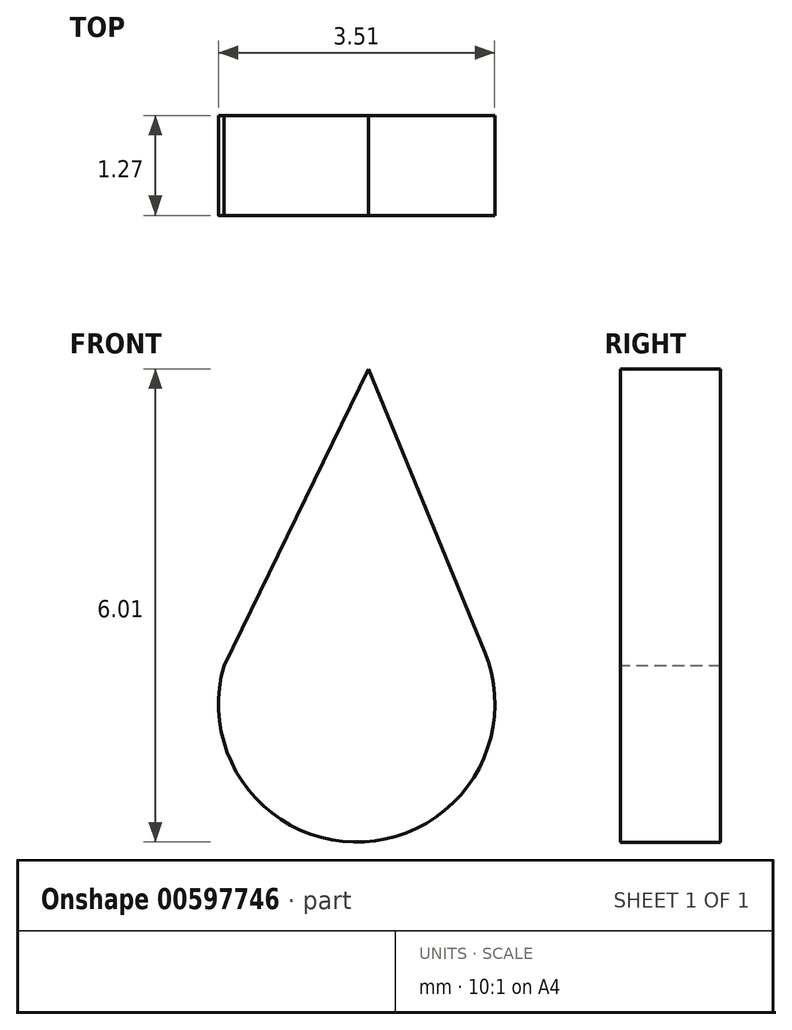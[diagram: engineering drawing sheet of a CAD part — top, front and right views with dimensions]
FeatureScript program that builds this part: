
annotation { "Feature Type Name" : "Feature", "Feature Type Description" : "" }
export const myFeature = defineFeature(function(context is Context, id is Id, definition is map)
    precondition{}
    {
        {
            var Q0;
            Q0=qCreatedBy(makeId("Front.planeOp"),FACE);
            var sketch = newSketch(context, id + "F0", { "sketchPlane" : qUnion([Q0])});
            skLineSegment(sketch, "E0", {"start": v(-28.52, -10.95) * mm, "end": v(-26.68, -7.18) * mm});
            skLineSegment(sketch, "E1", {"start": v(-26.68, -7.18) * mm, "end": v(-25.2, -10.77) * mm});
            skArc(sketch, "E2", {"start": v(-28.52, -10.95) * mm, "mid": v(-26.74, -13.19) * mm, "end": v(-25.2, -10.77) * mm});
            skSolve(sketch);
        }
        {
            var Q0;
            Q0=makeQuery(id+"F0.imprint","IMPRINT",FACE,{"disambiguationData":[TD([[makeQuery(id+"F0.imprint","IMPRINT",EDGE,{"derivedFrom":sQuery(id+"F0.wireOp",EDGE,"E0")}),-1.0]])]});
            extrude(context, id + "F1", {"entities" : qUnion([Q0]), "oppositeDirection" : true, "depth" : 1.27 * mm, "offsetDistance" : 25.4 * mm});
        }
    });
